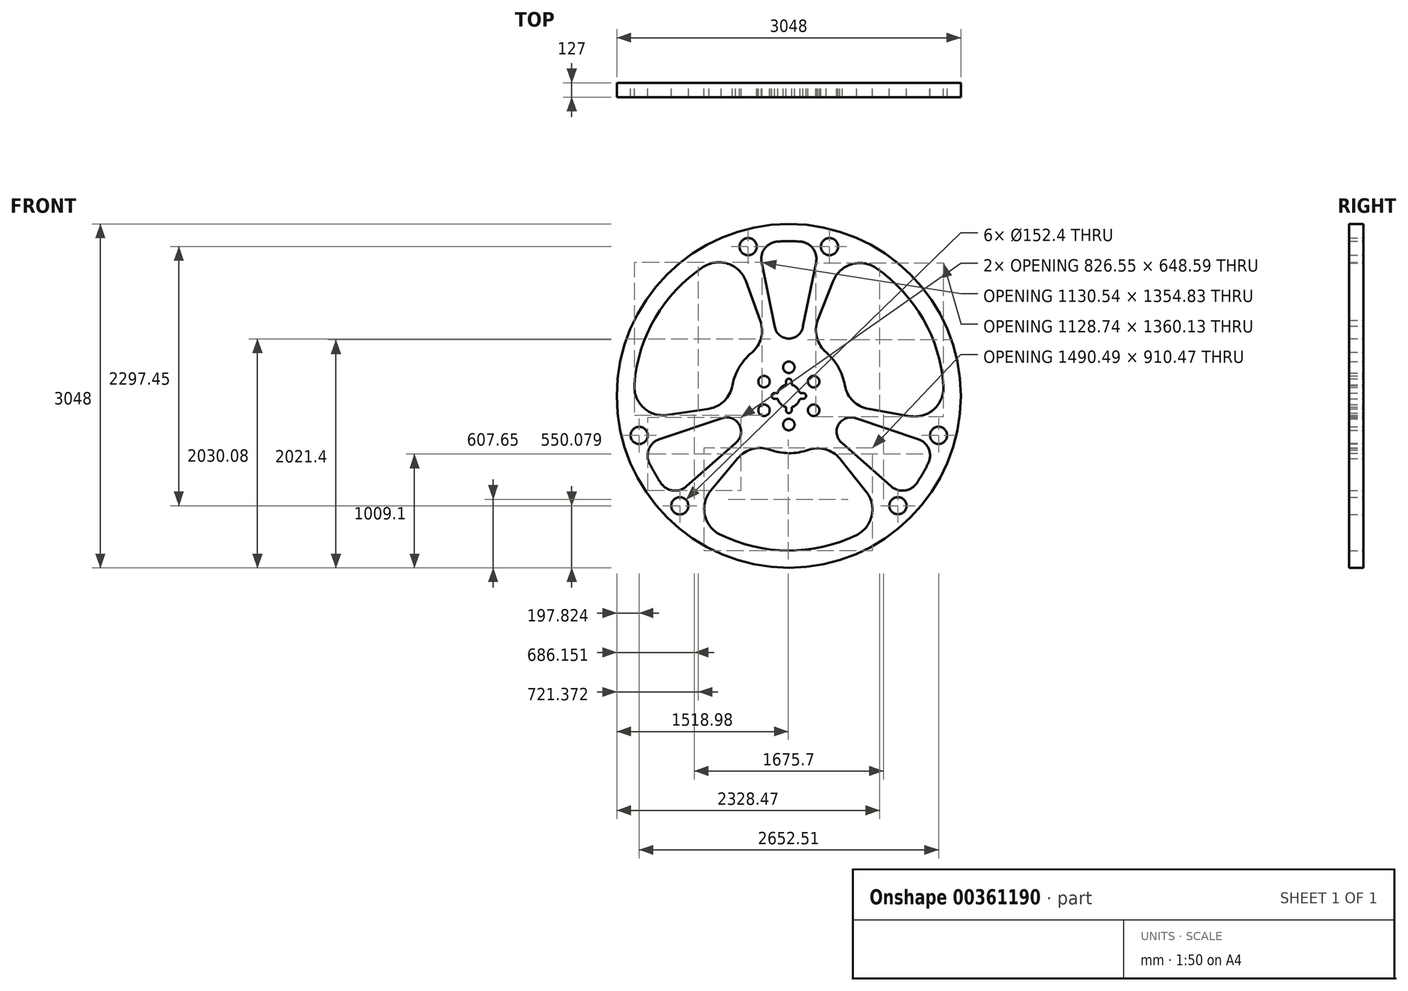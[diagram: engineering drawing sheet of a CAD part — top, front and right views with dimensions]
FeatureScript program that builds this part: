
annotation { "Feature Type Name" : "Feature", "Feature Type Description" : "" }
export const myFeature = defineFeature(function(context is Context, id is Id, definition is map)
    precondition{}
    {
        {
            var Q0;
            Q0=qCreatedBy(makeId("Front.planeOp"),FACE);
            var sketch = newSketch(context, id + "F0", { "sketchPlane" : qUnion([Q0])});
            skCircle(sketch, "E0", {"center": v(0, 0) * mm, "radius": 1524 * mm});
            skArc(sketch, "E1", {"start": v(103.3, 1367.7) * mm, "mid": v(0, 1371.6) * mm, "end": v(-103.3, 1367.7) * mm});
            skLineSegment(sketch, "E2", {"start": v(-122.05, 599.87) * mm, "end": v(-241.16, 1185.35) * mm});
            skLineSegment(sketch, "E3", {"start": v(122.05, 599.87) * mm, "end": v(241.16, 1185.35) * mm});
            skArc(sketch, "E4", {"start": v(-103.3, 1367.7) * mm, "mid": v(-213.39, 1307.65) * mm, "end": v(-241.16, 1185.35) * mm});
            skArc(sketch, "E5", {"start": v(241.16, 1185.35) * mm, "mid": v(213.39, 1307.65) * mm, "end": v(103.3, 1367.7) * mm});
            skArc(sketch, "E6", {"start": v(-126.07, 619.65) * mm, "mid": v(0, 508) * mm, "end": v(126.07, 619.65) * mm});
            skPoint(sketch, "E7.trimOffspring.start.orphan", {"position": v(0, 1337.37) * mm});
            skPoint(sketch, "E8.centerSnap0", {"position": v(-213.39, 1307.65) * mm});
            skCircle(sketch, "E9", {"center": v(359.93, 1323.53) * mm, "radius": 76.2 * mm});
            skCircle(sketch, "E10", {"center": v(-360.54, 1323.37) * mm, "radius": 76.2 * mm});
            skArc(sketch, "E11", {"start": v(-1236.12, -594.4) * mm, "mid": v(-1187.84, -685.8) * mm, "end": v(-1132.82, -773.31) * mm});
            skLineSegment(sketch, "E12.1.0", {"start": v(-580.53, -194.24) * mm, "end": v(-1147.13, -383.82) * mm});
            skArc(sketch, "E12.1.1", {"start": v(-473.6, -419) * mm, "mid": v(-439.94, -254) * mm, "end": v(-599.66, -200.64) * mm});
            skLineSegment(sketch, "E12.1.2", {"start": v(-458.48, -405.63) * mm, "end": v(-905.96, -801.53) * mm});
            skArc(sketch, "E12.1.3", {"start": v(-1132.82, -773.31) * mm, "mid": v(-1025.76, -838.62) * mm, "end": v(-905.96, -801.53) * mm});
            skArc(sketch, "E12.1.5", {"start": v(-1147.13, -383.82) * mm, "mid": v(-1239.15, -469.02) * mm, "end": v(-1236.12, -594.4) * mm});
            skCircle(sketch, "E12.1.6", {"center": v(-1326.18, -350.06) * mm, "radius": 76.2 * mm});
            skCircle(sketch, "E12.1.7", {"center": v(-965.8, -973.92) * mm, "radius": 76.2 * mm});
            skLineSegment(sketch, "E12.2.0", {"start": v(458.48, -405.63) * mm, "end": v(905.96, -801.53) * mm});
            skArc(sketch, "E12.2.1", {"start": v(599.66, -200.64) * mm, "mid": v(439.94, -254) * mm, "end": v(473.6, -419) * mm});
            skLineSegment(sketch, "E12.2.2", {"start": v(580.53, -194.24) * mm, "end": v(1147.13, -383.82) * mm});
            skArc(sketch, "E12.2.3", {"start": v(1236.12, -594.4) * mm, "mid": v(1239.15, -469.02) * mm, "end": v(1147.13, -383.82) * mm});
            skArc(sketch, "E12.2.5", {"start": v(905.96, -801.53) * mm, "mid": v(1025.76, -838.62) * mm, "end": v(1132.82, -773.31) * mm});
            skCircle(sketch, "E12.2.6", {"center": v(966.25, -973.47) * mm, "radius": 76.2 * mm});
            skCircle(sketch, "E12.2.7", {"center": v(1326.34, -349.45) * mm, "radius": 76.2 * mm});
            skArc(sketch, "E13", {"start": v(-169.16, -476.26) * mm, "mid": v(-322.9, -469.82) * mm, "end": v(-452.15, -553.33) * mm});
            skArc(sketch, "E14", {"start": v(-692.28, -839.8) * mm, "mid": v(-744.67, -1054.47) * mm, "end": v(-609.08, -1228.95) * mm});
            skArc(sketch, "E15", {"start": v(452.38, -556.63) * mm, "mid": v(323.14, -473.12) * mm, "end": v(169.4, -479.56) * mm});
            skArc(sketch, "E16", {"start": v(596.74, -1234.99) * mm, "mid": v(734.07, -1061.9) * mm, "end": v(683.86, -846.73) * mm});
            skLineSegment(sketch, "E17.trimOffspring", {"start": v(-452.15, -553.33) * mm, "end": v(-692.28, -839.8) * mm});
            skLineSegment(sketch, "E18.trimOffspring", {"start": v(452.38, -556.63) * mm, "end": v(683.86, -846.73) * mm});
            skLineSegment(sketch, "E19.trimOffspring", {"start": v(0, 1337.37) * mm, "end": v(0, 1371.6) * mm});
            skArc(sketch, "E20.trimOffspring", {"start": v(-169.16, -476.26) * mm, "mid": v(-0.16, -506.94) * mm, "end": v(169.4, -479.56) * mm});
            skArc(sketch, "E21.1.0", {"start": v(497.03, 91.63) * mm, "mid": v(439.1, 253.33) * mm, "end": v(330.6, 386.48) * mm});
            skArc(sketch, "E21.1.1", {"start": v(255.86, 670.1) * mm, "mid": v(248.16, 516.4) * mm, "end": v(330.6, 386.48) * mm});
            skLineSegment(sketch, "E21.1.2", {"start": v(255.86, 670.1) * mm, "end": v(391.36, 1015.6) * mm});
            skArc(sketch, "E21.1.3", {"start": v(771.16, 1134.28) * mm, "mid": v(552.6, 1166.67) * mm, "end": v(391.36, 1015.6) * mm});
            skArc(sketch, "E21.1.4", {"start": v(1073.43, -179.63) * mm, "mid": v(1285.53, -117.67) * mm, "end": v(1368.84, 87) * mm});
            skLineSegment(sketch, "E21.1.5", {"start": v(705.27, -114.9) * mm, "end": v(1073.43, -179.63) * mm});
            skArc(sketch, "E21.1.6", {"start": v(497.03, 91.63) * mm, "mid": v(568.33, -44.73) * mm, "end": v(705.27, -114.9) * mm});
            skArc(sketch, "E21.2.0", {"start": v(-327.87, 384.63) * mm, "mid": v(-438.94, 253.61) * mm, "end": v(-500, 93.07) * mm});
            skArc(sketch, "E21.2.1", {"start": v(-708.25, -113.46) * mm, "mid": v(-571.3, -43.29) * mm, "end": v(-500, 93.07) * mm});
            skLineSegment(sketch, "E21.2.2", {"start": v(-708.25, -113.46) * mm, "end": v(-1075.22, -168.88) * mm});
            skArc(sketch, "E21.2.3", {"start": v(-1367.9, 100.7) * mm, "mid": v(-1286.66, -104.77) * mm, "end": v(-1075.22, -168.88) * mm});
            skArc(sketch, "E21.2.4", {"start": v(-381.15, 1019.43) * mm, "mid": v(-540.86, 1172.14) * mm, "end": v(-759.76, 1141.95) * mm});
            skLineSegment(sketch, "E21.2.5", {"start": v(-253.12, 668.24) * mm, "end": v(-381.15, 1019.43) * mm});
            skArc(sketch, "E21.2.6", {"start": v(-327.87, 384.63) * mm, "mid": v(-245.43, 514.55) * mm, "end": v(-253.12, 668.24) * mm});
            skArc(sketch, "E22.trimOffspring", {"start": v(-609.08, -1228.95) * mm, "mid": v(-6.87, -1371.58) * mm, "end": v(596.74, -1234.99) * mm});
            skArc(sketch, "E23.trimOffspring", {"start": v(-759.76, 1141.95) * mm, "mid": v(-1184.4, 691.74) * mm, "end": v(-1367.9, 100.7) * mm});
            skArc(sketch, "E24.trimOffspring", {"start": v(1368.84, 87) * mm, "mid": v(1191.26, 679.84) * mm, "end": v(771.16, 1134.28) * mm});
            skArc(sketch, "E25.trimOffspring", {"start": v(1132.82, -773.31) * mm, "mid": v(1187.84, -685.8) * mm, "end": v(1236.12, -594.4) * mm});
            skCircle(sketch, "E26", {"center": v(0, 0) * mm, "radius": 381 * mm});
            skArc(sketch, "E27", {"start": v(-98.37, -25.4) * mm, "mid": v(-71.84, -71.84) * mm, "end": v(-25.4, -98.37) * mm});
            skPoint(sketch, "E28.centerSnap0", {"position": v(0, 508) * mm});
            skCircle(sketch, "E29", {"center": v(-0.16, -254) * mm, "radius": 50.8 * mm});
            skPoint(sketch, "E29.centerSnap0", {"position": v(-0.16, -506.94) * mm});
            skCircle(sketch, "E30", {"center": v(0, 254) * mm, "radius": 50.8 * mm});
            skCircle(sketch, "E31.1.0", {"center": v(220.05, 126.86) * mm, "radius": 50.8 * mm});
            skCircle(sketch, "E31.1.1", {"center": v(-219.97, -127) * mm, "radius": 50.8 * mm});
            skCircle(sketch, "E31.2.0", {"center": v(-219.89, 127.14) * mm, "radius": 50.8 * mm});
            skCircle(sketch, "E31.2.1", {"center": v(219.97, -127) * mm, "radius": 50.8 * mm});
            skArc(sketch, "E32", {"start": v(-127, 25.4) * mm, "mid": v(-152.4, 0) * mm, "end": v(-127, -25.4) * mm});
            skArc(sketch, "E33", {"start": v(127, -25.4) * mm, "mid": v(152.4, 0) * mm, "end": v(127, 25.4) * mm});
            skArc(sketch, "E34", {"start": v(25.4, 127) * mm, "mid": v(0, 152.4) * mm, "end": v(-25.4, 127) * mm});
            skArc(sketch, "E35", {"start": v(-25.4, -127) * mm, "mid": v(0, -152.4) * mm, "end": v(25.4, -127) * mm});
            skLineSegment(sketch, "E36", {"start": v(-25.4, -127) * mm, "end": v(-25.4, -98.37) * mm});
            skLineSegment(sketch, "E37", {"start": v(25.4, -127) * mm, "end": v(25.4, -98.37) * mm});
            skLineSegment(sketch, "E38", {"start": v(127, -25.4) * mm, "end": v(98.37, -25.4) * mm});
            skLineSegment(sketch, "E39", {"start": v(127, 25.4) * mm, "end": v(98.37, 25.4) * mm});
            skLineSegment(sketch, "E40", {"start": v(25.4, 127) * mm, "end": v(25.4, 98.37) * mm});
            skLineSegment(sketch, "E41", {"start": v(-25.4, 127) * mm, "end": v(-25.4, 98.37) * mm});
            skLineSegment(sketch, "E42", {"start": v(-127, 25.4) * mm, "end": v(-98.37, 25.4) * mm});
            skLineSegment(sketch, "E43", {"start": v(-127, -25.4) * mm, "end": v(-98.37, -25.4) * mm});
            skArc(sketch, "E44.trimOffspring", {"start": v(98.37, 25.4) * mm, "mid": v(71.84, 71.84) * mm, "end": v(25.4, 98.37) * mm});
            skArc(sketch, "E45.trimOffspring", {"start": v(-25.4, 98.37) * mm, "mid": v(-71.84, 71.84) * mm, "end": v(-98.37, 25.4) * mm});
            skArc(sketch, "E46.trimOffspring", {"start": v(25.4, -98.37) * mm, "mid": v(71.84, -71.84) * mm, "end": v(98.37, -25.4) * mm});
            skSolve(sketch);
        }
        {
            var Q0;
            Q0=makeQuery(id+"F0.imprint","IMPRINT",FACE,{"disambiguationData":[TD([[makeQuery(id+"F0.imprint","IMPRINT",EDGE,{"derivedFrom":sQuery(id+"F0.wireOp",EDGE,"E0")}),1.0]])]});
            var Q1;
            Q1=makeQuery(id+"F0.imprint","IMPRINT",FACE,{"disambiguationData":[TD([[makeQuery(id+"F0.imprint","IMPRINT",EDGE,{"derivedFrom":sQuery(id+"F0.wireOp",EDGE,"E26")}),1.0]])]});
            extrude(context, id + "F1", {"entities" : qUnion([Q0, Q1]), "depth" : 127 * mm});
        }
    });
